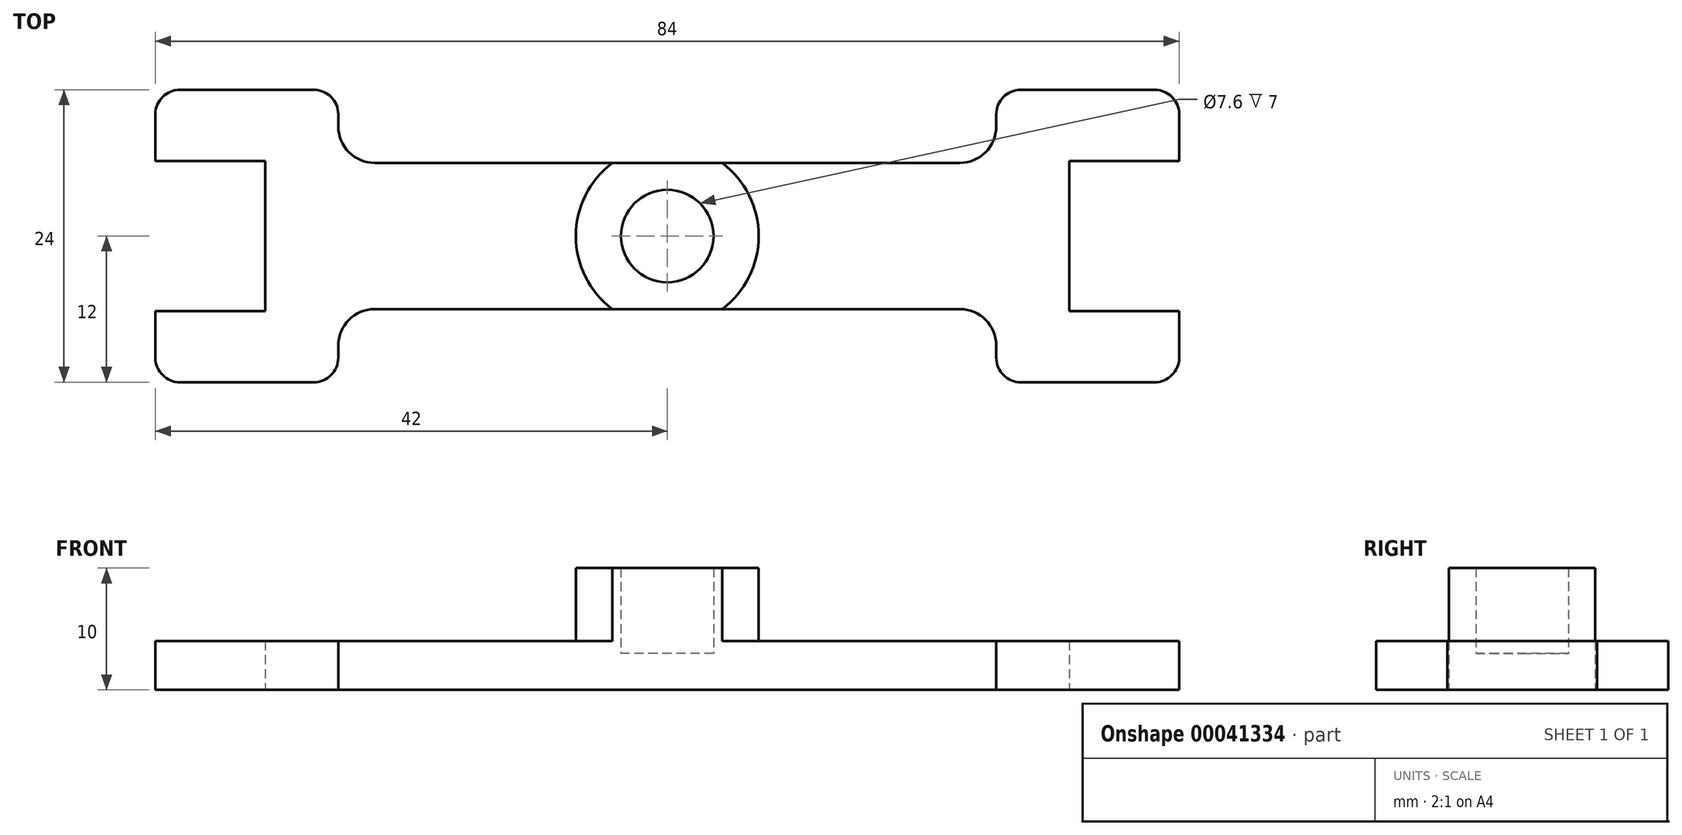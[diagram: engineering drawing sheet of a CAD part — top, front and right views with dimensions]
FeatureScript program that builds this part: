
annotation { "Feature Type Name" : "Feature", "Feature Type Description" : "" }
export const myFeature = defineFeature(function(context is Context, id is Id, definition is map)
    precondition{}
    {
        {
            var Q0;
            Q0=qCreatedBy(makeId("Top.planeOp"),FACE);
            var sketch = newSketch(context, id + "F0", { "sketchPlane" : qUnion([Q0])});
            skLineSegment(sketch, "E0.rect.bottom", {"start": v(24, 6) * mm, "end": v(-24, 6) * mm});
            skLineSegment(sketch, "E0.rect.left", {"start": v(42, 6) * mm, "end": v(42, -6) * mm});
            skLineSegment(sketch, "E0.rect.right", {"start": v(-42, 6) * mm, "end": v(-42, -6) * mm});
            skPoint(sketch, "E0.rect.middle", {"position": v(0, 0) * mm});
            skLineSegment(sketch, "E1.bottom", {"start": v(40, -12) * mm, "end": v(29, -12) * mm});
            skLineSegment(sketch, "E1.top", {"start": v(40, 12) * mm, "end": v(29, 12) * mm});
            skLineSegment(sketch, "E1.left", {"start": v(42, -10) * mm, "end": v(42, 10) * mm});
            skLineSegment(sketch, "E1.right", {"start": v(27, -10) * mm, "end": v(27, -9) * mm});
            skLineSegment(sketch, "E2.bottom", {"start": v(-40, -12) * mm, "end": v(-29, -12) * mm});
            skLineSegment(sketch, "E2.top", {"start": v(-40, 12) * mm, "end": v(-29, 12) * mm});
            skLineSegment(sketch, "E2.left", {"start": v(-42, -10) * mm, "end": v(-42, 10) * mm});
            skLineSegment(sketch, "E2.right", {"start": v(-27, -10) * mm, "end": v(-27, -9) * mm});
            skLineSegment(sketch, "E3.rect.bottom", {"start": v(-33, 6.15) * mm, "end": v(-42, 6.15) * mm});
            skLineSegment(sketch, "E3.rect.top", {"start": v(-33, -6.15) * mm, "end": v(-42, -6.15) * mm});
            skLineSegment(sketch, "E3.rect.left", {"start": v(-33, 6.15) * mm, "end": v(-33, -6.15) * mm});
            skPoint(sketch, "E3.rect.middle", {"position": v(-42, 0) * mm});
            skLineSegment(sketch, "E4.rect.bottom", {"start": v(33, 6.15) * mm, "end": v(42, 6.15) * mm});
            skLineSegment(sketch, "E4.rect.top", {"start": v(33, -6.15) * mm, "end": v(42, -6.15) * mm});
            skLineSegment(sketch, "E4.rect.left", {"start": v(33, 6.15) * mm, "end": v(33, -6.15) * mm});
            skPoint(sketch, "E4.rect.middle", {"position": v(42, 0) * mm});
            skLineSegment(sketch, "E5.trimOffspring", {"start": v(24, -6) * mm, "end": v(-24, -6) * mm});
            skPoint(sketch, "E4.rect.right.start.orphan", {"position": v(51, 6.15) * mm});
            skPoint(sketch, "E6.orphan", {"position": v(51, -6.15) * mm});
            skPoint(sketch, "E3.rect.right.end.orphan", {"position": v(-51, -6.15) * mm});
            skPoint(sketch, "E3.rect.right.start.orphan", {"position": v(-51, 6.15) * mm});
            skLineSegment(sketch, "E7.trimOffspring", {"start": v(-27, 9) * mm, "end": v(-27, 10) * mm});
            skLineSegment(sketch, "E8.trimOffspring", {"start": v(27, 9) * mm, "end": v(27, 10) * mm});
            skPoint(sketch, "E9.visualSharp", {"position": v(27, 6) * mm});
            skArc(sketch, "E9.filletArc", {"start": v(24, 6) * mm, "mid": v(26.12, 6.88) * mm, "end": v(27, 9) * mm});
            skPoint(sketch, "E10.visualSharp", {"position": v(27, -6) * mm});
            skArc(sketch, "E10.filletArc", {"start": v(27, -9) * mm, "mid": v(26.12, -6.88) * mm, "end": v(24, -6) * mm});
            skPoint(sketch, "E11.visualSharp", {"position": v(-27, -6) * mm});
            skArc(sketch, "E11.filletArc", {"start": v(-24, -6) * mm, "mid": v(-26.12, -6.88) * mm, "end": v(-27, -9) * mm});
            skPoint(sketch, "E12.visualSharp", {"position": v(-27, 6) * mm});
            skArc(sketch, "E12.filletArc", {"start": v(-27, 9) * mm, "mid": v(-26.12, 6.88) * mm, "end": v(-24, 6) * mm});
            skPoint(sketch, "E13.visualSharp", {"position": v(27, 12) * mm});
            skArc(sketch, "E13.filletArc", {"start": v(29, 12) * mm, "mid": v(27.59, 11.41) * mm, "end": v(27, 10) * mm});
            skPoint(sketch, "E14.visualSharp", {"position": v(42, 12) * mm});
            skArc(sketch, "E14.filletArc", {"start": v(42, 10) * mm, "mid": v(41.41, 11.41) * mm, "end": v(40, 12) * mm});
            skPoint(sketch, "E15.visualSharp", {"position": v(42, -12) * mm});
            skArc(sketch, "E15.filletArc", {"start": v(40, -12) * mm, "mid": v(41.41, -11.41) * mm, "end": v(42, -10) * mm});
            skPoint(sketch, "E16.visualSharp", {"position": v(27, -12) * mm});
            skArc(sketch, "E16.filletArc", {"start": v(27, -10) * mm, "mid": v(27.59, -11.41) * mm, "end": v(29, -12) * mm});
            skPoint(sketch, "E17.visualSharp", {"position": v(-27, -12) * mm});
            skArc(sketch, "E17.filletArc", {"start": v(-29, -12) * mm, "mid": v(-27.59, -11.41) * mm, "end": v(-27, -10) * mm});
            skPoint(sketch, "E18.visualSharp", {"position": v(-42, -12) * mm});
            skArc(sketch, "E18.filletArc", {"start": v(-42, -10) * mm, "mid": v(-41.41, -11.41) * mm, "end": v(-40, -12) * mm});
            skPoint(sketch, "E19.visualSharp", {"position": v(-42, 12) * mm});
            skArc(sketch, "E19.filletArc", {"start": v(-40, 12) * mm, "mid": v(-41.41, 11.41) * mm, "end": v(-42, 10) * mm});
            skPoint(sketch, "E20.visualSharp", {"position": v(-27, 12) * mm});
            skArc(sketch, "E20.filletArc", {"start": v(-27, 10) * mm, "mid": v(-27.59, 11.41) * mm, "end": v(-29, 12) * mm});
            skCircle(sketch, "E21", {"center": v(0, 0) * mm, "radius": 7.5 * mm});
            skCircle(sketch, "E22", {"center": v(0, 0) * mm, "radius": 3.8 * mm});
            skSolve(sketch);
        }
        {
            var Q0;
            Q0=makeQuery(id+"F0.imprint","IMPRINT",FACE,{"disambiguationData":[TD([[makeQuery(id+"F0.imprint","IMPRINT",EDGE,{"derivedFrom":sQuery(id+"F0.wireOp",EDGE,"E22")}),-1.0]])]});
            var Q1;
            {var subQ0=sQuery(id+"F0.wireOp",EDGE,"E21");var subQ1=sQuery(id+"F0.wireOp",EDGE,"E5.trimOffspring");var subQ3=makeQuery(id+"F0.imprint","INTERSECT",VERTEX,{"disambiguationData":[OD(0.0)],"derivedFrom":[subQ1,subQ0]});Q1=makeQuery(id+"F0.imprint","IMPRINT",FACE,{"disambiguationData":[TD([[makeQuery(id+"F0.imprint","IMPRINT",EDGE,{"disambiguationData":[TD([[subQ3,-1.0]])],"derivedFrom":subQ1}),1.0]])]});}
            var Q2;
            {var subQ0=sQuery(id+"F0.wireOp",EDGE,"E21");var subQ1=sQuery(id+"F0.wireOp",EDGE,"E0.rect.bottom");var subQ3=makeQuery(id+"F0.imprint","INTERSECT",VERTEX,{"disambiguationData":[OD(0.0)],"derivedFrom":[subQ1,subQ0]});Q2=makeQuery(id+"F0.imprint","IMPRINT",FACE,{"disambiguationData":[TD([[makeQuery(id+"F0.imprint","IMPRINT",EDGE,{"disambiguationData":[TD([[subQ3,-1.0]])],"derivedFrom":subQ1}),-1.0]])]});}
            extrude(context, id + "F1", {"entities" : qUnion([Q0, Q1, Q2]), "depth" : 10 * mm});
        }
        {
            var Q0;
            Q0=makeQuery(id+"F0.imprint","IMPRINT",FACE,{"disambiguationData":[TD([[makeQuery(id+"F0.imprint","IMPRINT",EDGE,{"derivedFrom":sQuery(id+"F0.wireOp",EDGE,"E2.bottom")}),1.0]])]});
            var Q1;
            Q1=makeQuery(id+"F0.imprint","IMPRINT",FACE,{"disambiguationData":[TD([[makeQuery(id+"F0.imprint","IMPRINT",EDGE,{"derivedFrom":sQuery(id+"F0.wireOp",EDGE,"E1.bottom")}),-1.0]])]});
            extrude(context, id + "F2", {"entities" : qUnion([Q0, Q1]), "operationType" : NewBodyOperationType.ADD, "depth" : 4 * mm});
        }
        {
            var Q0;
            Q0=makeQuery(id+"F0.imprint","IMPRINT",FACE,{"disambiguationData":[TD([[makeQuery(id+"F0.imprint","IMPRINT",EDGE,{"derivedFrom":sQuery(id+"F0.wireOp",EDGE,"E22")}),1.0]])]});
            extrude(context, id + "F3", {"entities" : qUnion([Q0]), "operationType" : NewBodyOperationType.ADD, "depth" : 3 * mm});
        }
    });
